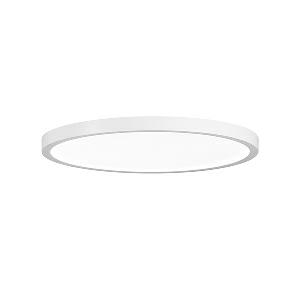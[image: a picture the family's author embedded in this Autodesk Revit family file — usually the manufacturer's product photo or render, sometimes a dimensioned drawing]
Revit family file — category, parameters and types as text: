
# Revit family: vivaa_fit_-_via_7000_vtl_d_00813055_7ece
name_source: partatom
category: Lighting Fixtures
units: mm (PartAtom-declared; Revit-internal decimal feet)

## family parameters
Cut with Voids When Loaded = No
Host = Face
Light Source = No
Part Type = Normal
Room Calculation Point = No
Round Connector Dimension = Use Diameter
Shared = No

## types (1)
- VIVAA.fit - VIA 7000/VTL/D (1 x LED, 6700 lm, 2700-6500K)
    Apparent Load = 61 VA
    Approval mark = CE
    CIE Flux Codes = 66 90 97 41 100
    Color Rendering = 90-100
    Color Temperature = 2700-6500K
    Control Gear = Electronic ballast
    Default Elevation = 1800 mm
    Description = VIA 7000/VTL/D|Surface-mounted luminaire.|light source:      |work equipment: Power supply unit|luminous flux: 6700 lm|light distribution: Direct/indirect|class of protection: I|mains lead: Direct power supply 5 pin|glare control: optical film|special features: Specified values at approx. 4000 K, Biodynamic light VTL, External control device required for DALI Device Type 6, Separated, direct and indirect light individually adjustable|
    Frequency = 50 Hz, 60 Hz
    Height = 48 mm  [stored 0.15748 ft]
    Lamp = 1 x LED
    Lamp Light Flux = 6700 lm
    Lamp count = 1
    Length = 450 mm
    Luminous efficacy = 110 lm/W
    Manufacturer = Waldmann
    ModVariant = No
    Model = 00813055
    Mounting Place = Ceiling
    Mounting Type = Surface mounted
    Number of Poles = 1
    OnlyDefault = Yes
    Power Factor = 1
    Product Name = VIVAA.fit - VIA 7000/VTL/D
    Product group = Ceiling mounted luminaire
    ProductGroupID = 3
    Protection Class = Protection class I
    Protection Degree = Degree of protection
    RLX_Detail_Level = 1
    RLX_Emergency_Light_Flux = 0 lm
    RLX_Emergency_Type = 0
    RLX_Emergency_Type_DB = No
    RlxData = <blob elided: 20685 chars, md5=b29cb27d>
    Socket = socket
    Standby Power = 0 W
    System Light Flux = 6700 lm
    System Power = 61 W
    Type Comments = Product without accessories
    Type Image = vivaa_2.0_anbau_450mm.jpg
    URL = http://relux.com
    VarID = ---
    Voltage = 230 V
    Voltage Range = 220-240 V
    Weight = 0.00 kg
    Width = 0 mm  [stored 0 ft]

note: [stored X ft] marks values corroborated as IEEE doubles in the binary element streams (Revit-internal decimal feet)

## geometry (parser evidence)
native form markers: Blend x4, Sweep x12
no freeform markers — native parametric forms only
